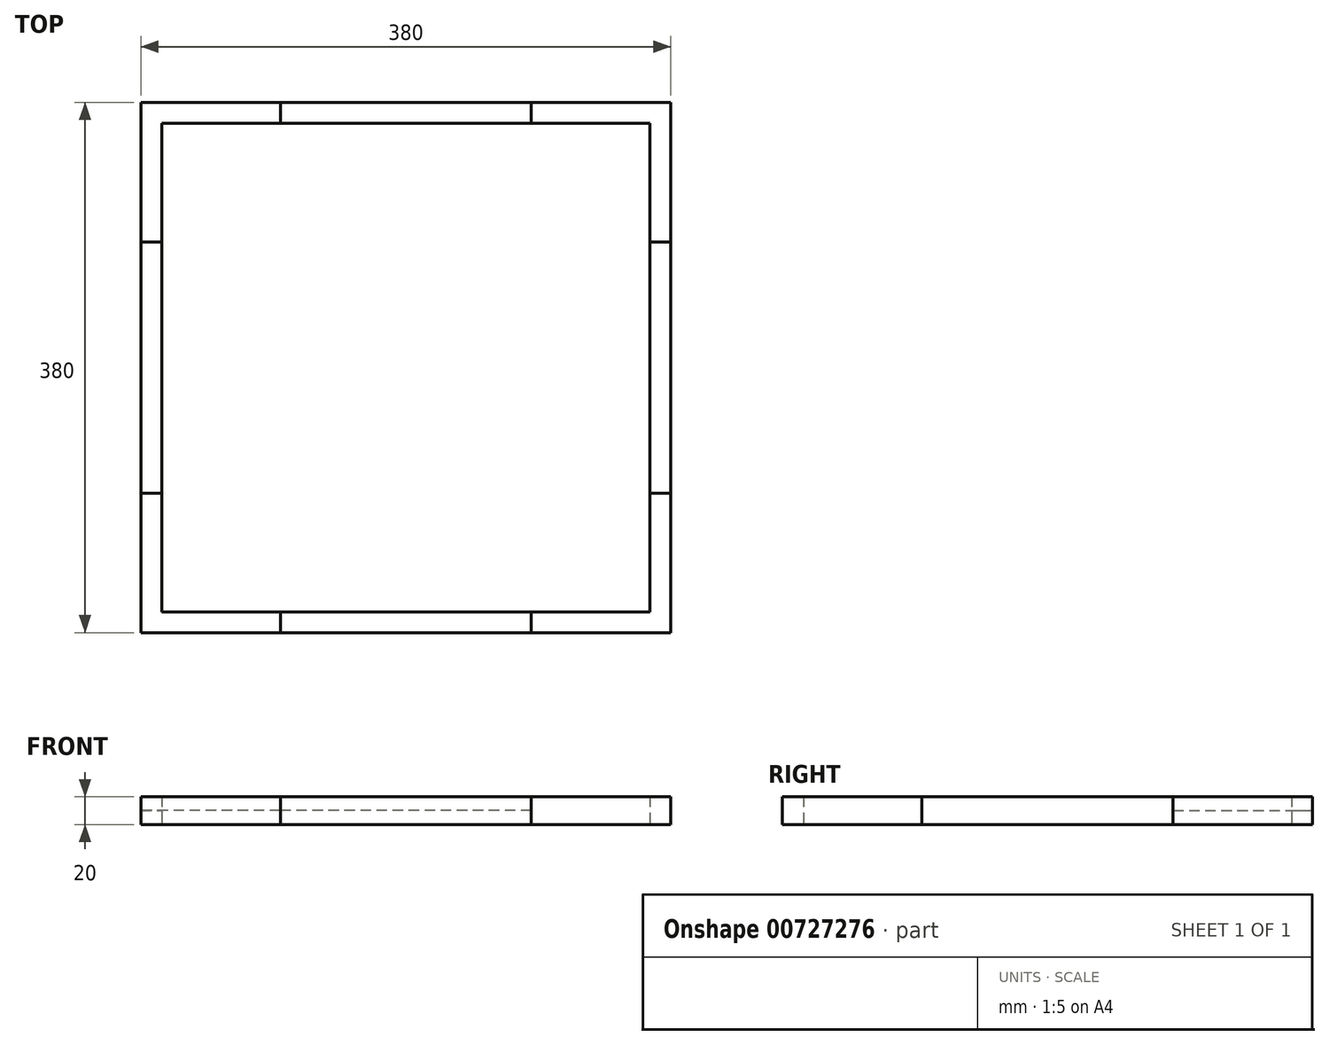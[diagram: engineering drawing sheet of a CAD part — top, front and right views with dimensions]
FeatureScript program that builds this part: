
annotation { "Feature Type Name" : "Feature", "Feature Type Description" : "" }
export const myFeature = defineFeature(function(context is Context, id is Id, definition is map)
    precondition{}
    {
        {
            var Q0;
            Q0=qCreatedBy(makeId("Top.planeOp"),FACE);
            var sketch = newSketch(context, id + "F0", { "sketchPlane" : qUnion([Q0])});
            skLineSegment(sketch, "E0.bottom", {"start": v(175, -175) * mm, "end": v(-175, -175) * mm});
            skLineSegment(sketch, "E0.top", {"start": v(175, 175) * mm, "end": v(-175, 175) * mm});
            skLineSegment(sketch, "E0.left", {"start": v(175, -175) * mm, "end": v(175, 175) * mm});
            skLineSegment(sketch, "E0.right", {"start": v(-175, -175) * mm, "end": v(-175, 175) * mm});
            skPoint(sketch, "E0.middle", {"position": v(0, 0) * mm});
            skLineSegment(sketch, "E1.bottom", {"start": v(190, -190) * mm, "end": v(-190, -190) * mm});
            skLineSegment(sketch, "E1.top", {"start": v(190, 190) * mm, "end": v(-190, 190) * mm});
            skLineSegment(sketch, "E1.left", {"start": v(190, -190) * mm, "end": v(190, 190) * mm});
            skLineSegment(sketch, "E1.right", {"start": v(-190, -190) * mm, "end": v(-190, 190) * mm});
            skLineSegment(sketch, "E2", {"start": v(-90, 190) * mm, "end": v(-90, -190) * mm});
            skLineSegment(sketch, "E3", {"start": v(90, -190) * mm, "end": v(90, 190) * mm});
            skLineSegment(sketch, "E4", {"start": v(-190, 90) * mm, "end": v(190, 90) * mm});
            skLineSegment(sketch, "E5", {"start": v(-190, -90) * mm, "end": v(190, -90) * mm});
            skSolve(sketch);
        }
        {
            var Q0;
            {var subQ5=sQuery(id+"F0.wireOp",EDGE,"E0.right");var subQ9=sQuery(id+"F0.wireOp",EDGE,"E0.top");var subQ10=makeQuery(id+"F0.imprint","INTERSECT",VERTEX,{"derivedFrom":[subQ9,subQ5]});Q0=makeQuery(id+"F0.imprint","IMPRINT",FACE,{"disambiguationData":[TD([[makeQuery(id+"F0.imprint","IMPRINT",EDGE,{"disambiguationData":[TD([[subQ10,1.0]])],"derivedFrom":subQ9}),-1.0]])]});}
            extrude(context, id + "F1", {"entities" : qUnion([Q0]), "depth" : 10 * mm, "offsetDistance" : 25 * mm});
        }
        {
            var Q0;
            {var subQ0=sQuery(id+"F0.wireOp",EDGE,"E3");var subQ1=sQuery(id+"F0.wireOp",EDGE,"E0.top");var subQ2=makeQuery(id+"F0.imprint","INTERSECT",VERTEX,{"derivedFrom":[subQ1,subQ0]});Q0=makeQuery(id+"F0.imprint","IMPRINT",FACE,{"disambiguationData":[TD([[makeQuery(id+"F0.imprint","IMPRINT",EDGE,{"disambiguationData":[TD([[subQ2,-1.0]])],"derivedFrom":subQ1}),-1.0]])]});}
            extrude(context, id + "F2", {"entities" : qUnion([Q0]), "depth" : 10 * mm, "offsetDistance" : 25 * mm});
        }
        {
            var Q0;
            {var subQ7=sQuery(id+"F0.wireOp",EDGE,"E0.left");var subQ8=sQuery(id+"F0.wireOp",EDGE,"E0.top");var subQ9=makeQuery(id+"F0.imprint","INTERSECT",VERTEX,{"derivedFrom":[subQ8,subQ7]});Q0=makeQuery(id+"F0.imprint","IMPRINT",FACE,{"disambiguationData":[TD([[makeQuery(id+"F0.imprint","IMPRINT",EDGE,{"disambiguationData":[TD([[subQ9,-1.0]])],"derivedFrom":subQ8}),-1.0]])]});}
            extrude(context, id + "F3", {"entities" : qUnion([Q0]), "depth" : 20 * mm, "offsetDistance" : 25 * mm});
        }
        {
            var Q0;
            {var subQ0=sQuery(id+"F0.wireOp",EDGE,"E5");var subQ1=sQuery(id+"F0.wireOp",EDGE,"E0.right");var subQ2=makeQuery(id+"F0.imprint","INTERSECT",VERTEX,{"derivedFrom":[subQ1,subQ0]});Q0=makeQuery(id+"F0.imprint","IMPRINT",FACE,{"disambiguationData":[TD([[makeQuery(id+"F0.imprint","IMPRINT",EDGE,{"disambiguationData":[TD([[subQ2,-1.0]])],"derivedFrom":subQ1}),1.0]])]});}
            extrude(context, id + "F4", {"entities" : qUnion([Q0]), "depth" : 20 * mm, "offsetDistance" : 25 * mm});
        }
        {
            var Q0;
            {var subQ7=sQuery(id+"F0.wireOp",EDGE,"E0.right");var subQ8=sQuery(id+"F0.wireOp",EDGE,"E0.bottom");var subQ9=makeQuery(id+"F0.imprint","INTERSECT",VERTEX,{"derivedFrom":[subQ8,subQ7]});Q0=makeQuery(id+"F0.imprint","IMPRINT",FACE,{"disambiguationData":[TD([[makeQuery(id+"F0.imprint","IMPRINT",EDGE,{"disambiguationData":[TD([[subQ9,1.0]])],"derivedFrom":subQ8}),1.0]])]});}
            extrude(context, id + "F5", {"entities" : qUnion([Q0]), "depth" : 20 * mm, "offsetDistance" : 25 * mm});
        }
        {
            var Q0;
            {var subQ0=sQuery(id+"F0.wireOp",EDGE,"E3");var subQ1=sQuery(id+"F0.wireOp",EDGE,"E0.bottom");var subQ2=makeQuery(id+"F0.imprint","INTERSECT",VERTEX,{"derivedFrom":[subQ1,subQ0]});Q0=makeQuery(id+"F0.imprint","IMPRINT",FACE,{"disambiguationData":[TD([[makeQuery(id+"F0.imprint","IMPRINT",EDGE,{"disambiguationData":[TD([[subQ2,-1.0]])],"derivedFrom":subQ1}),1.0]])]});}
            extrude(context, id + "F6", {"entities" : qUnion([Q0]), "depth" : 20 * mm, "offsetDistance" : 25 * mm});
        }
        {
            var Q0;
            {var subQ7=sQuery(id+"F0.wireOp",EDGE,"E0.bottom");var subQ9=sQuery(id+"F0.wireOp",EDGE,"E0.left");var subQ10=makeQuery(id+"F0.imprint","INTERSECT",VERTEX,{"derivedFrom":[subQ7,subQ9]});Q0=makeQuery(id+"F0.imprint","IMPRINT",FACE,{"disambiguationData":[TD([[makeQuery(id+"F0.imprint","IMPRINT",EDGE,{"disambiguationData":[TD([[subQ10,-1.0]])],"derivedFrom":subQ7}),1.0]])]});}
            extrude(context, id + "F7", {"entities" : qUnion([Q0]), "depth" : 20 * mm, "offsetDistance" : 25 * mm});
        }
        {
            var Q0;
            {var subQ0=sQuery(id+"F0.wireOp",EDGE,"E5");var subQ1=sQuery(id+"F0.wireOp",EDGE,"E0.left");var subQ2=makeQuery(id+"F0.imprint","INTERSECT",VERTEX,{"derivedFrom":[subQ1,subQ0]});Q0=makeQuery(id+"F0.imprint","IMPRINT",FACE,{"disambiguationData":[TD([[makeQuery(id+"F0.imprint","IMPRINT",EDGE,{"disambiguationData":[TD([[subQ2,-1.0]])],"derivedFrom":subQ1}),-1.0]])]});}
            extrude(context, id + "F8", {"entities" : qUnion([Q0]), "depth" : 20 * mm, "offsetDistance" : 25 * mm});
        }
    });
